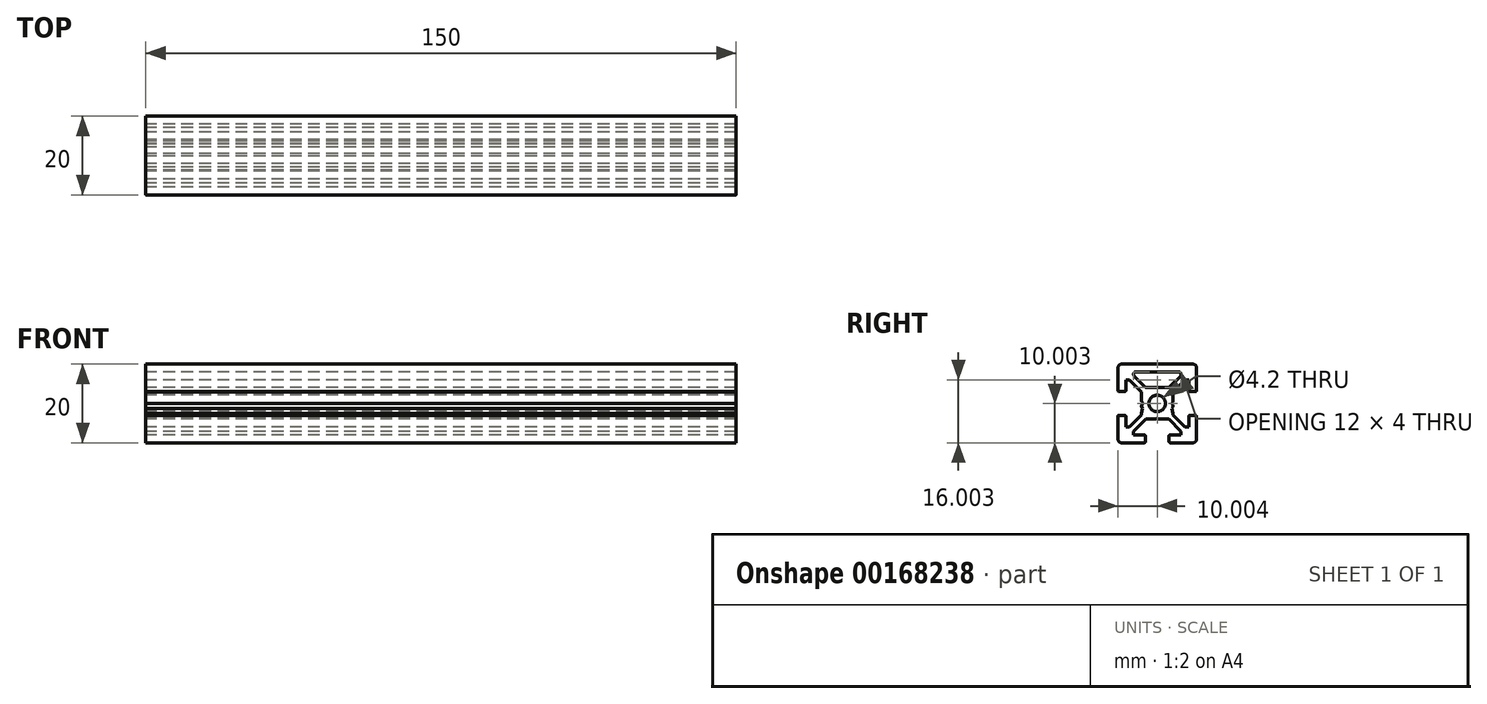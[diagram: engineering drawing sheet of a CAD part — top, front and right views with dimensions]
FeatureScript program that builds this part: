
annotation { "Feature Type Name" : "Feature", "Feature Type Description" : "" }
export const myFeature = defineFeature(function(context is Context, id is Id, definition is map)
    precondition{}
    {
        {
            var Q0;
            Q0=qCreatedBy(makeId("Right.planeOp"),FACE);
            var sketch = newSketch(context, id + "F0", { "sketchPlane" : qUnion([Q0])});
            skLineSegment(sketch, "E0", {"start": v(0.04, 10.07) * mm, "end": v(-8.96, 10.07) * mm});
            skLineSegment(sketch, "E1", {"start": v(-9.96, 9.07) * mm, "end": v(-9.96, 3.37) * mm});
            skLineSegment(sketch, "E2", {"start": v(-3.96, 3.01) * mm, "end": v(-3.96, 0.73) * mm});
            skLineSegment(sketch, "E3", {"start": v(0.04, 4.07) * mm, "end": v(-2.69, 4.07) * mm});
            skLineSegment(sketch, "E4", {"start": v(0.04, 8.07) * mm, "end": v(-5.46, 8.07) * mm});
            skLineSegment(sketch, "E5", {"start": v(-7.96, 6.07) * mm, "end": v(-7.96, 3.37) * mm});
            skLineSegment(sketch, "E6", {"start": v(-8.26, 3.07) * mm, "end": v(-9.66, 3.07) * mm});
            skLineSegment(sketch, "E7", {"start": v(-8.26, -2.93) * mm, "end": v(-9.66, -2.93) * mm});
            skLineSegment(sketch, "E8", {"start": v(-7.02, -5.93) * mm, "end": v(-7.96, -5.93) * mm});
            skLineSegment(sketch, "E9", {"start": v(-7.96, -3.23) * mm, "end": v(-7.96, -5.93) * mm});
            skLineSegment(sketch, "E10", {"start": v(-9.96, -3.23) * mm, "end": v(-9.96, -8.93) * mm});
            skLineSegment(sketch, "E11", {"start": v(-7.02, 6.07) * mm, "end": v(-7.96, 6.07) * mm});
            skLineSegment(sketch, "E12", {"start": v(-3.89, -0.33) * mm, "end": v(-3.66, 0.07) * mm});
            skLineSegment(sketch, "E13", {"start": v(-3.89, 0.48) * mm, "end": v(-3.66, 0.07) * mm});
            skLineSegment(sketch, "E14", {"start": v(-3.96, -2.43) * mm, "end": v(-3.96, -2.87) * mm});
            skLineSegment(sketch, "E15", {"start": v(-3.96, 3.01) * mm, "end": v(-7.02, 6.07) * mm});
            skLineSegment(sketch, "E16", {"start": v(-3.96, -2.87) * mm, "end": v(-7.02, -5.93) * mm});
            skLineSegment(sketch, "E17", {"start": v(-3.96, -2.43) * mm, "end": v(-3.7, -1.15) * mm});
            skArc(sketch, "E18", {"start": v(-3.89, -0.33) * mm, "mid": v(-3.96, -0.58) * mm, "end": v(-3.89, -0.83) * mm});
            skLineSegment(sketch, "E19", {"start": v(-3.89, -0.83) * mm, "end": v(-3.7, -1.15) * mm});
            skArc(sketch, "E20", {"start": v(-3.96, 0.73) * mm, "mid": v(-3.94, 0.6) * mm, "end": v(-3.89, 0.48) * mm});
            skArc(sketch, "E21", {"start": v(-8.26, 3.07) * mm, "mid": v(-8.04, 3.16) * mm, "end": v(-7.96, 3.37) * mm});
            skArc(sketch, "E22", {"start": v(-9.96, 3.37) * mm, "mid": v(-9.87, 3.16) * mm, "end": v(-9.66, 3.07) * mm});
            skArc(sketch, "E23", {"start": v(-7.96, -3.23) * mm, "mid": v(-8.04, -3.01) * mm, "end": v(-8.26, -2.93) * mm});
            skArc(sketch, "E24", {"start": v(-9.66, -2.93) * mm, "mid": v(-9.87, -3.01) * mm, "end": v(-9.96, -3.23) * mm});
            skLineSegment(sketch, "E25", {"start": v(-2.9, -3.93) * mm, "end": v(-0.61, -3.93) * mm});
            skArc(sketch, "E26", {"start": v(-3.26, -9.93) * mm, "mid": v(-3.04, -9.84) * mm, "end": v(-2.96, -9.63) * mm});
            skLineSegment(sketch, "E27", {"start": v(-5.96, -7.93) * mm, "end": v(-3.26, -7.93) * mm});
            skArc(sketch, "E28", {"start": v(-2.96, -8.23) * mm, "mid": v(-3.04, -8.01) * mm, "end": v(-3.26, -7.93) * mm});
            skLineSegment(sketch, "E29", {"start": v(-5.96, -6.99) * mm, "end": v(-5.96, -7.93) * mm});
            skLineSegment(sketch, "E30", {"start": v(-2.96, -8.23) * mm, "end": v(-2.96, -9.63) * mm});
            skLineSegment(sketch, "E31", {"start": v(-0.36, -3.86) * mm, "end": v(-0.06, -3.69) * mm});
            skArc(sketch, "E32", {"start": v(-0.61, -3.93) * mm, "mid": v(-0.48, -3.9) * mm, "end": v(-0.36, -3.86) * mm});
            skLineSegment(sketch, "E33", {"start": v(-2.9, -3.93) * mm, "end": v(-5.96, -6.99) * mm});
            skLineSegment(sketch, "E34", {"start": v(-3.26, -9.93) * mm, "end": v(-8.96, -9.93) * mm});
            skLineSegment(sketch, "E35", {"start": v(-3.04, 4.22) * mm, "end": v(-5.8, 6.99) * mm});
            skLineSegment(sketch, "E36", {"start": v(-5.96, 7.57) * mm, "end": v(-5.96, 7.34) * mm});
            skArc(sketch, "E37", {"start": v(0.04, -2.03) * mm, "mid": v(-2.06, 0.07) * mm, "end": v(0.04, 2.17) * mm});
            skArc(sketch, "E38", {"start": v(-9.96, -8.93) * mm, "mid": v(-9.66, -9.63) * mm, "end": v(-8.96, -9.93) * mm});
            skArc(sketch, "E39", {"start": v(-8.96, 10.07) * mm, "mid": v(-9.66, 9.78) * mm, "end": v(-9.96, 9.07) * mm});
            skArc(sketch, "E40", {"start": v(-5.46, 8.07) * mm, "mid": v(-5.8, 7.93) * mm, "end": v(-5.96, 7.57) * mm});
            skArc(sketch, "E41", {"start": v(-5.96, 7.34) * mm, "mid": v(-5.92, 7.15) * mm, "end": v(-5.8, 6.99) * mm});
            skArc(sketch, "E42", {"start": v(-3.04, 4.22) * mm, "mid": v(-2.88, 4.11) * mm, "end": v(-2.69, 4.07) * mm});
            skArc(sketch, "E43.MirrorCS", {"start": v(8.34, 3.07) * mm, "mid": v(8.13, 3.16) * mm, "end": v(8.04, 3.37) * mm});
            skArc(sketch, "E44.MirrorCS", {"start": v(5.54, 8.07) * mm, "mid": v(5.9, 7.93) * mm, "end": v(6.04, 7.57) * mm});
            skLineSegment(sketch, "E45.MirrorCS", {"start": v(3.98, -0.33) * mm, "end": v(3.74, 0.07) * mm});
            skArc(sketch, "E46.MirrorCS", {"start": v(3.04, -8.23) * mm, "mid": v(3.13, -8.01) * mm, "end": v(3.34, -7.93) * mm});
            skLineSegment(sketch, "E47.MirrorCS", {"start": v(3.98, -0.83) * mm, "end": v(3.8, -1.15) * mm});
            skArc(sketch, "E48.MirrorCS", {"start": v(3.34, -9.93) * mm, "mid": v(3.13, -9.84) * mm, "end": v(3.04, -9.63) * mm});
            skLineSegment(sketch, "E49.MirrorCS", {"start": v(7.1, -5.93) * mm, "end": v(8.04, -5.93) * mm});
            skArc(sketch, "E50.MirrorCS", {"start": v(3.98, -0.33) * mm, "mid": v(4.04, -0.58) * mm, "end": v(3.98, -0.83) * mm});
            skLineSegment(sketch, "E51.MirrorCS", {"start": v(4.04, -2.43) * mm, "end": v(3.8, -1.15) * mm});
            skArc(sketch, "E52.MirrorCS", {"start": v(9.74, -2.93) * mm, "mid": v(9.96, -3.01) * mm, "end": v(10.04, -3.23) * mm});
            skArc(sketch, "E53.MirrorCS", {"start": v(0.7, -3.93) * mm, "mid": v(0.63, -3.92) * mm, "end": v(0.57, -3.91) * mm});
            skLineSegment(sketch, "E54.MirrorCS", {"start": v(6.04, 7.57) * mm, "end": v(6.04, 7.34) * mm});
            skLineSegment(sketch, "E55.MirrorCS", {"start": v(6.04, -6.99) * mm, "end": v(6.04, -7.93) * mm});
            skArc(sketch, "E56.MirrorCS", {"start": v(6.04, 7.34) * mm, "mid": v(6, 7.15) * mm, "end": v(5.9, 6.99) * mm});
            skArc(sketch, "E57.MirrorCS", {"start": v(4.04, 0.73) * mm, "mid": v(4.03, 0.6) * mm, "end": v(3.98, 0.48) * mm});
            skArc(sketch, "E58.MirrorCS", {"start": v(8.04, -3.23) * mm, "mid": v(8.13, -3.01) * mm, "end": v(8.34, -2.93) * mm});
            skArc(sketch, "E59.MirrorCS", {"start": v(10.04, 3.37) * mm, "mid": v(9.96, 3.16) * mm, "end": v(9.74, 3.07) * mm});
            skArc(sketch, "E60.MirrorCS", {"start": v(3.13, 4.22) * mm, "mid": v(2.97, 4.11) * mm, "end": v(2.78, 4.07) * mm});
            skLineSegment(sketch, "E61.MirrorCS", {"start": v(7.1, 6.07) * mm, "end": v(8.04, 6.07) * mm});
            skLineSegment(sketch, "E62.MirrorCS", {"start": v(4.04, -2.43) * mm, "end": v(4.04, -2.87) * mm});
            skLineSegment(sketch, "E63.MirrorCS", {"start": v(3.98, 0.48) * mm, "end": v(3.74, 0.07) * mm});
            skLineSegment(sketch, "E64.MirrorCS", {"start": v(3.04, -8.23) * mm, "end": v(3.04, -9.63) * mm});
            skLineSegment(sketch, "E65.MirrorCS", {"start": v(3.13, 4.22) * mm, "end": v(5.9, 6.99) * mm});
            skLineSegment(sketch, "E66.MirrorCS", {"start": v(10.04, -3.23) * mm, "end": v(10.04, -8.93) * mm});
            skLineSegment(sketch, "E67.MirrorCS", {"start": v(8.04, -3.23) * mm, "end": v(8.04, -5.93) * mm});
            skLineSegment(sketch, "E68.MirrorCS", {"start": v(8.34, -2.93) * mm, "end": v(9.74, -2.93) * mm});
            skLineSegment(sketch, "E69.MirrorCS", {"start": v(8.34, 3.07) * mm, "end": v(9.74, 3.07) * mm});
            skLineSegment(sketch, "E70.MirrorCS", {"start": v(2.98, -3.93) * mm, "end": v(0.7, -3.93) * mm});
            skLineSegment(sketch, "E71.MirrorCS", {"start": v(4.04, 3.01) * mm, "end": v(4.04, 0.73) * mm});
            skLineSegment(sketch, "E72.MirrorCS", {"start": v(4.04, -2.87) * mm, "end": v(7.1, -5.93) * mm});
            skLineSegment(sketch, "E73.MirrorCS", {"start": v(2.98, -3.93) * mm, "end": v(6.04, -6.99) * mm});
            skArc(sketch, "E74.MirrorCS", {"start": v(9.04, 10.07) * mm, "mid": v(9.75, 9.78) * mm, "end": v(10.04, 9.07) * mm});
            skLineSegment(sketch, "E75.MirrorCS", {"start": v(6.04, -7.93) * mm, "end": v(3.34, -7.93) * mm});
            skLineSegment(sketch, "E76.MirrorCS", {"start": v(4.04, 3.01) * mm, "end": v(7.1, 6.07) * mm});
            skArc(sketch, "E77.MirrorCS", {"start": v(10.04, -8.93) * mm, "mid": v(9.75, -9.63) * mm, "end": v(9.04, -9.93) * mm});
            skLineSegment(sketch, "E78.MirrorCS", {"start": v(3.34, -9.93) * mm, "end": v(9.04, -9.93) * mm});
            skLineSegment(sketch, "E79.MirrorCS", {"start": v(8.04, 6.07) * mm, "end": v(8.04, 3.37) * mm});
            skLineSegment(sketch, "E80.MirrorCS", {"start": v(10.04, 9.07) * mm, "end": v(10.04, 3.37) * mm});
            skLineSegment(sketch, "E81.MirrorCS", {"start": v(0.04, 10.07) * mm, "end": v(9.04, 10.07) * mm});
            skLineSegment(sketch, "E82.MirrorCS", {"start": v(0.04, 8.07) * mm, "end": v(5.54, 8.07) * mm});
            skLineSegment(sketch, "E83.MirrorCS", {"start": v(0.04, 4.07) * mm, "end": v(2.78, 4.07) * mm});
            skArc(sketch, "E84.MirrorCS", {"start": v(0.04, -2.03) * mm, "mid": v(2.14, 0.07) * mm, "end": v(0.04, 2.17) * mm});
            skLineSegment(sketch, "E85", {"start": v(0.22, -3.85) * mm, "end": v(-0.06, -3.69) * mm});
            skArc(sketch, "E86", {"start": v(0.22, -3.85) * mm, "mid": v(0.4, -3.92) * mm, "end": v(0.57, -3.91) * mm});
            skSolve(sketch);
        }
        {
            var Q0;
            Q0 = qSketchRegion(id + "F0", true);
            extrude(context, id + "F1", {"entities" : qUnion([Q0]), "endBound" : BoundingType.SYMMETRIC, "depth" : 150 * mm});
        }
    });
